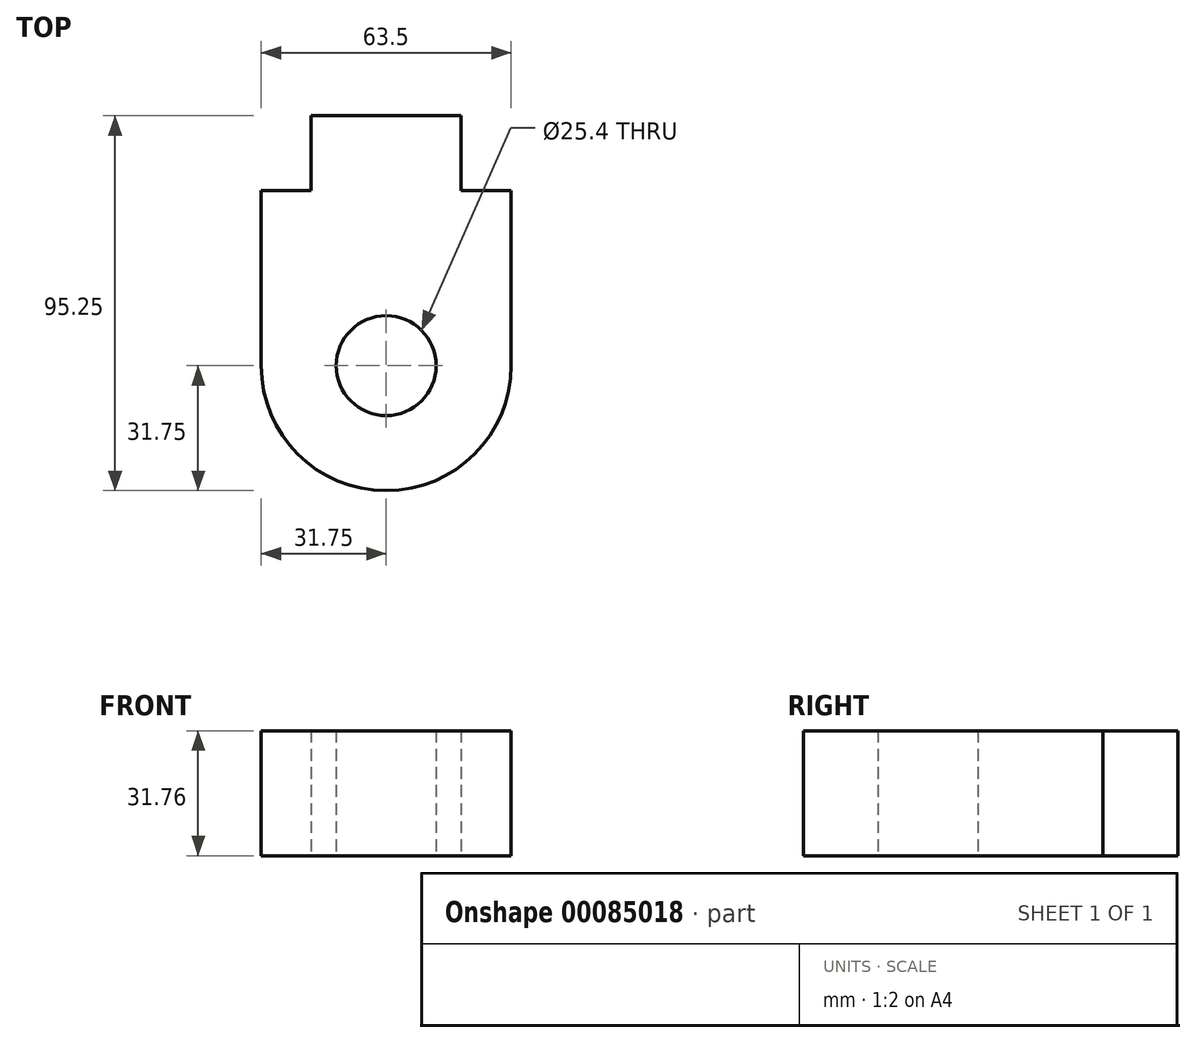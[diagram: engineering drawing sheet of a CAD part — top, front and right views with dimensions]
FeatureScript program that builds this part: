
annotation { "Feature Type Name" : "Feature", "Feature Type Description" : "" }
export const myFeature = defineFeature(function(context is Context, id is Id, definition is map)
    precondition{}
    {
        {
            var Q0;
            Q0=qCreatedBy(makeId("Top.planeOp"),FACE);
            var sketch = newSketch(context, id + "F0", { "sketchPlane" : qUnion([Q0])});
            skLineSegment(sketch, "E0", {"start": v(-19.05, 63.5) * mm, "end": v(19.05, 63.5) * mm});
            skLineSegment(sketch, "E1", {"start": v(19.05, 63.5) * mm, "end": v(19.05, 44.45) * mm});
            skLineSegment(sketch, "E2", {"start": v(19.05, 44.45) * mm, "end": v(31.75, 44.45) * mm});
            skLineSegment(sketch, "E3", {"start": v(31.75, 44.45) * mm, "end": v(31.75, 0) * mm});
            skArc(sketch, "E4", {"start": v(31.75, 0) * mm, "mid": v(0, -31.75) * mm, "end": v(-31.75, 0) * mm});
            skLineSegment(sketch, "E5", {"start": v(-31.75, 0) * mm, "end": v(-31.75, 44.45) * mm});
            skLineSegment(sketch, "E6", {"start": v(-31.75, 44.45) * mm, "end": v(-19.05, 44.45) * mm});
            skLineSegment(sketch, "E7", {"start": v(-19.05, 44.45) * mm, "end": v(-19.05, 63.5) * mm});
            skCircle(sketch, "E8", {"center": v(0, 0) * mm, "radius": 12.7 * mm});
            skSolve(sketch);
        }
        {
            var Q0;
            Q0=makeQuery(id+"F0.imprint","IMPRINT",FACE,{"disambiguationData":[TD([[makeQuery(id+"F0.imprint","IMPRINT",EDGE,{"derivedFrom":sQuery(id+"F0.wireOp",EDGE,"E0")}),-1.0]])]});
            extrude(context, id + "F1", {"entities" : qUnion([Q0]), "endBound" : BoundingType.SYMMETRIC, "depth" : 31.75 * mm, "offsetDistance" : 25.4 * mm});
        }
    });
